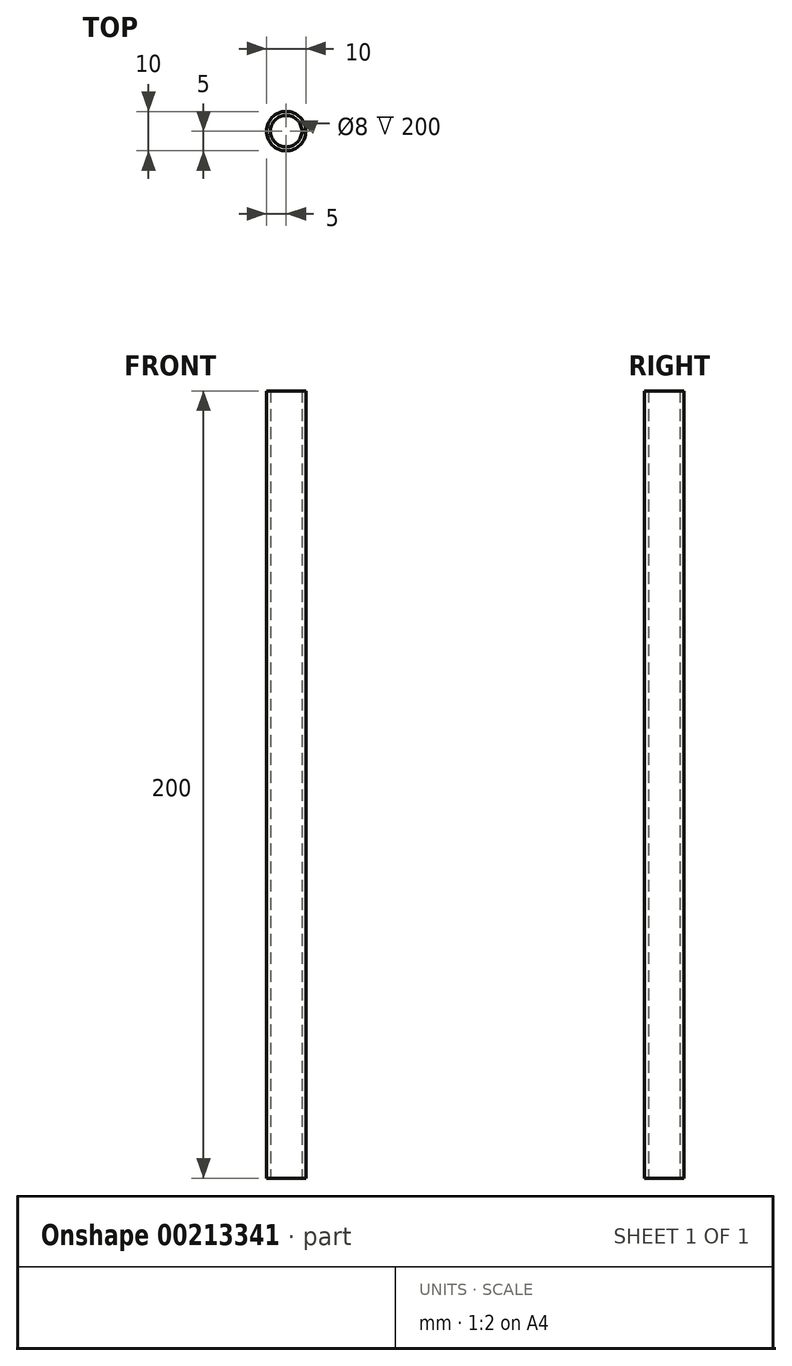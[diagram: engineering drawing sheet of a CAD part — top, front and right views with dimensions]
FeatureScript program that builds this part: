
annotation { "Feature Type Name" : "Feature", "Feature Type Description" : "" }
export const myFeature = defineFeature(function(context is Context, id is Id, definition is map)
    precondition{}
    {
        {
            var Q0;
            Q0=qCreatedBy(makeId("Top.planeOp"),FACE);
            var sketch = newSketch(context, id + "F0", { "sketchPlane" : qUnion([Q0])});
            skCircle(sketch, "E0", {"center": v(0, 0) * mm, "radius": 4 * mm});
            skCircle(sketch, "E1", {"center": v(0, 0) * mm, "radius": 5 * mm});
            skSolve(sketch);
        }
        {
            var Q0;
            Q0=makeQuery(id+"F0.imprint","IMPRINT",FACE,{"disambiguationData":[TD([[makeQuery(id+"F0.imprint","IMPRINT",EDGE,{"derivedFrom":sQuery(id+"F0.wireOp",EDGE,"E0")}),-1.0]])]});
            extrude(context, id + "F1", {"entities" : qUnion([Q0]), "depth" : 200 * mm});
        }
    });
